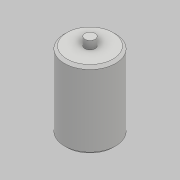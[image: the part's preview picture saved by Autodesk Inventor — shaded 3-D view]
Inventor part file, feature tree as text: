
AUTODESK INVENTOR PART (.ipt)
format: ipt  version: 2018 (Build 220112000, 112)  size: 96,256 bytes
history: native  units: mm
features: other x2, chamfer x1, sketch x1
ambient origin geometry x8: Origin, YZ Plane, XZ Plane, XY Plane, X Axis, Y Axis, Z Axis, Center Point
bodies: Body1 (feature_tree)
feature tree (4):
  other  "實體1"
  other  "迴轉1"
  chamfer  "倒角1"  Distance=50.0mm
  sketch  "草圖1"
